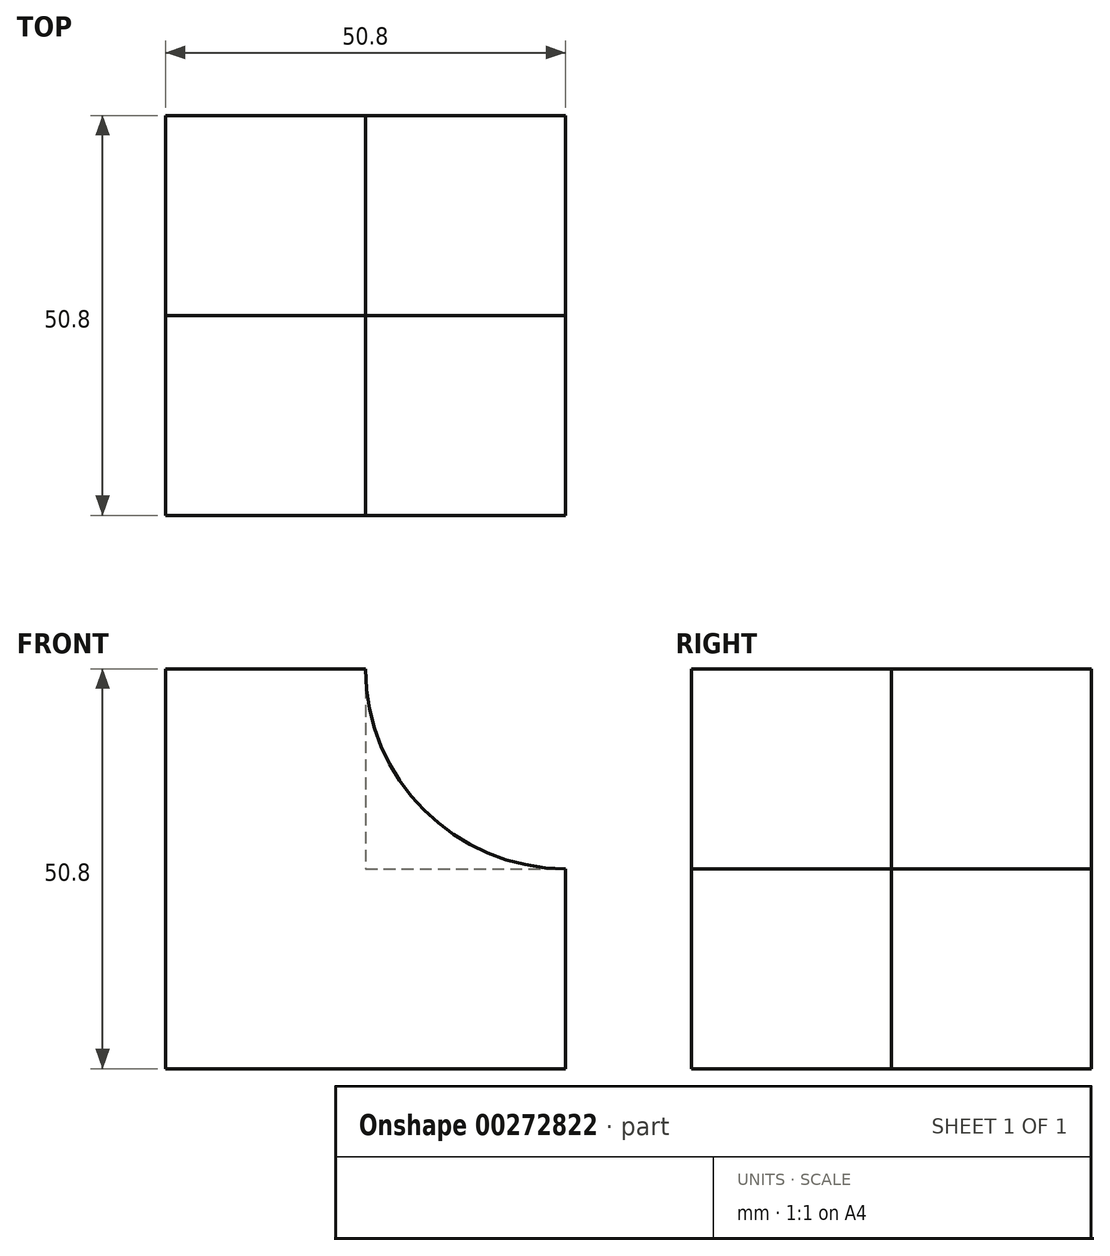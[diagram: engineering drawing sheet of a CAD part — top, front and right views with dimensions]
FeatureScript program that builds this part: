
annotation { "Feature Type Name" : "Feature", "Feature Type Description" : "" }
export const myFeature = defineFeature(function(context is Context, id is Id, definition is map)
    precondition{}
    {
        {
            var Q0;
            Q0=qCreatedBy(makeId("Front.planeOp"),FACE);
            var sketch = newSketch(context, id + "F0", { "sketchPlane" : qUnion([Q0])});
            skLineSegment(sketch, "E0", {"start": v(0, 0) * mm, "end": v(-50.8, 0) * mm});
            skLineSegment(sketch, "E1", {"start": v(-50.8, 0) * mm, "end": v(-50.8, 50.8) * mm});
            skLineSegment(sketch, "E2", {"start": v(-50.8, 50.8) * mm, "end": v(-25.4, 50.8) * mm});
            skLineSegment(sketch, "E3", {"start": v(-25.4, 50.8) * mm, "end": v(-25.4, 25.4) * mm});
            skLineSegment(sketch, "E4", {"start": v(-25.4, 25.4) * mm, "end": v(0, 25.4) * mm});
            skLineSegment(sketch, "E5", {"start": v(0, 25.4) * mm, "end": v(0, 0) * mm});
            skSolve(sketch);
        }
        {
            var Q0;
            Q0=makeQuery(id+"F0.imprint","IMPRINT",FACE,{"disambiguationData":[TD([[makeQuery(id+"F0.imprint","IMPRINT",EDGE,{"derivedFrom":sQuery(id+"F0.wireOp",EDGE,"E0")}),-1.0]])]});
            extrude(context, id + "F1", {"entities" : qUnion([Q0]), "depth" : 25.4 * mm});
        }
        {
            var Q0;
            Q0=makeQuery(id+"F1.opExtrude","CAP_FACE",FACE,{"disambiguationData":[OSD([sQuery(id+"F0.wireOp",EDGE,"E0"),sQuery(id+"F0.wireOp",EDGE,"E1"),sQuery(id+"F0.wireOp",EDGE,"E2"),sQuery(id+"F0.wireOp",EDGE,"E3"),sQuery(id+"F0.wireOp",EDGE,"E4"),sQuery(id+"F0.wireOp",EDGE,"E5")])],"isStart":false});
            var sketch = newSketch(context, id + "F2", { "sketchPlane" : qUnion([Q0])});
            skArc(sketch, "E6", {"start": v(-25.4, 50.8) * mm, "mid": v(-17.96, 32.84) * mm, "end": v(0, 25.4) * mm});
            skSolve(sketch);
        }
        {
            var Q0;
            Q0=makeQuery(id+"F2.imprint","IMPRINT",FACE,{"disambiguationData":[TD([[makeQuery(id+"F2.imprint","IMPRINT",EDGE,{"derivedFrom":makeQuery(id+"F1.opExtrude","CAP_EDGE",EDGE,{"disambiguationData":[OSD([sQuery(id+"F0.wireOp",EDGE,"E0")])],"isStart":false})}),-1.0]])]});
            var Q1;
            Q1=makeQuery(id+"F2.imprint","IMPRINT",FACE,{"disambiguationData":[TD([[makeQuery(id+"F2.imprint","IMPRINT",EDGE,{"derivedFrom":sQuery(id+"F2.wireOp",EDGE,"E6")}),-1.0]])]});
            extrude(context, id + "F3", {"entities" : qUnion([Q0, Q1]), "depth" : 25.4 * mm});
        }
    });
